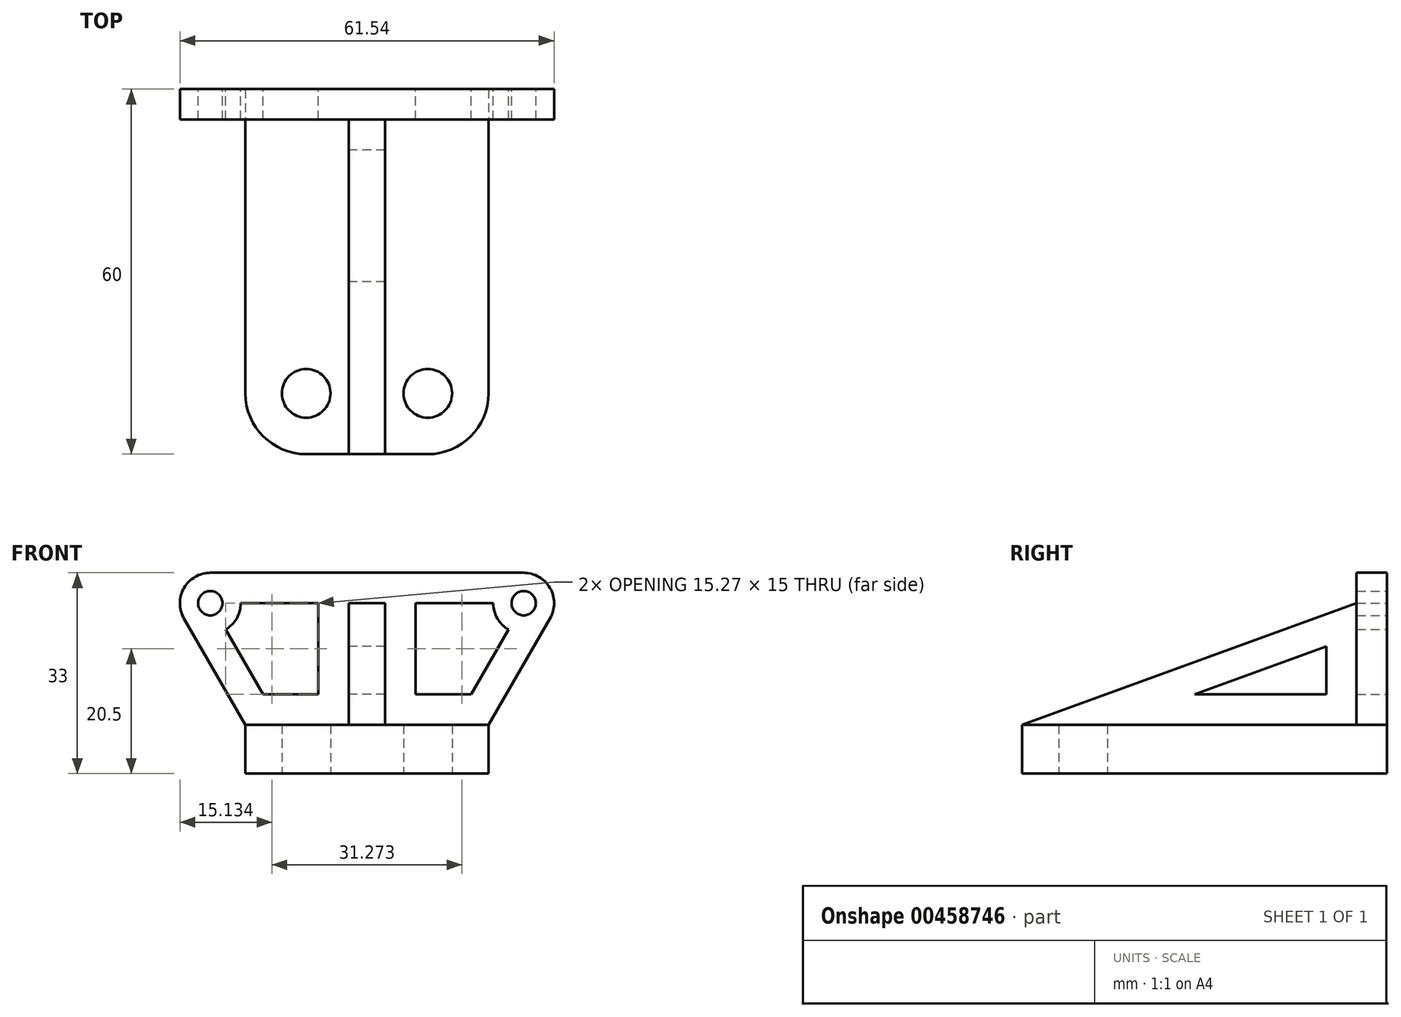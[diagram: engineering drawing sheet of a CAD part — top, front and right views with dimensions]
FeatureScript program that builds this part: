
annotation { "Feature Type Name" : "Feature", "Feature Type Description" : "" }
export const myFeature = defineFeature(function(context is Context, id is Id, definition is map)
    precondition{}
    {
        {
            var Q0;
            Q0=qCreatedBy(makeId("Top.planeOp"),FACE);
            var sketch = newSketch(context, id + "F0", { "sketchPlane" : qUnion([Q0])});
            skLineSegment(sketch, "E0.bottom", {"start": v(0, 0) * mm, "end": v(20, 0) * mm});
            skLineSegment(sketch, "E0.top", {"start": v(0, -60) * mm, "end": v(10, -60) * mm});
            skLineSegment(sketch, "E0.left", {"start": v(0, 0) * mm, "end": v(0, -60) * mm});
            skLineSegment(sketch, "E0.right", {"start": v(20, 0) * mm, "end": v(20, -50) * mm});
            skPoint(sketch, "E1.visualSharp", {"position": v(20, -60) * mm});
            skArc(sketch, "E1.filletArc", {"start": v(10, -60) * mm, "mid": v(17.07, -57.07) * mm, "end": v(20, -50) * mm});
            skCircle(sketch, "E2", {"center": v(10, -50) * mm, "radius": 4 * mm});
            skLineSegment(sketch, "E3.MirrorCS", {"start": v(0, 0) * mm, "end": v(-20, 0) * mm});
            skLineSegment(sketch, "E4.MirrorCS", {"start": v(-20, 0) * mm, "end": v(-20, -50) * mm});
            skCircle(sketch, "E5.MirrorC", {"center": v(-10, -50) * mm, "radius": 4 * mm});
            skLineSegment(sketch, "E6.MirrorCS", {"start": v(0, -60) * mm, "end": v(-10, -60) * mm});
            skArc(sketch, "E7.MirrorCS", {"start": v(-10, -60) * mm, "mid": v(-17.07, -57.07) * mm, "end": v(-20, -50) * mm});
            skSolve(sketch);
        }
        {
            var Q0;
            Q0 = qSketchRegion(id + "F0", true);
            extrude(context, id + "F1", {"entities" : qUnion([Q0]), "depth" : 8 * mm});
        }
        {
            var Q0;
            Q0=qCreatedBy(makeId("Front.planeOp"),FACE);
            var sketch = newSketch(context, id + "F2", { "sketchPlane" : qUnion([Q0])});
            skLineSegment(sketch, "E8.0", {"start": v(20, 8) * mm, "end": v(20, 0) * mm});
            skLineSegment(sketch, "E9.0", {"start": v(-20, 8) * mm, "end": v(20, 8) * mm});
            skLineSegment(sketch, "E10.0", {"start": v(-20, 0) * mm, "end": v(20, 0) * mm});
            skLineSegment(sketch, "E11.0", {"start": v(-20, 8) * mm, "end": v(-20, 0) * mm});
            skLineSegment(sketch, "E12", {"start": v(20, 8) * mm, "end": v(30.1, 25.5) * mm});
            skLineSegment(sketch, "E13", {"start": v(25.77, 33) * mm, "end": v(0, 33) * mm});
            skLineSegment(sketch, "E14", {"start": v(25.77, 28) * mm, "end": v(23.77, 28) * mm, "construction": true});
            skLineSegment(sketch, "E15", {"start": v(8, 28) * mm, "end": v(8, 13) * mm});
            skLineSegment(sketch, "E16", {"start": v(8, 13) * mm, "end": v(17.11, 13) * mm});
            skLineSegment(sketch, "E17", {"start": v(17.11, 13) * mm, "end": v(23.27, 23.67) * mm});
            skLineSegment(sketch, "E18", {"start": v(3, 28) * mm, "end": v(3, 8) * mm});
            skLineSegment(sketch, "E19", {"start": v(3, 28) * mm, "end": v(0, 28) * mm});
            skCircle(sketch, "E20", {"center": v(25.77, 28) * mm, "radius": 2 * mm});
            skPoint(sketch, "E21.visualSharp", {"position": v(34.43, 33) * mm});
            skArc(sketch, "E21.filletArc", {"start": v(30.1, 25.5) * mm, "mid": v(30.1, 30.5) * mm, "end": v(25.77, 33) * mm});
            skArc(sketch, "E22.0", {"start": v(20.77, 28) * mm, "mid": v(21.44, 25.5) * mm, "end": v(23.27, 23.67) * mm});
            skLineSegment(sketch, "E23.trimOffspring", {"start": v(20.77, 28) * mm, "end": v(8, 28) * mm});
            skLineSegment(sketch, "E24.MirrorCS", {"start": v(-25.77, 33) * mm, "end": v(0, 33) * mm});
            skLineSegment(sketch, "E25.MirrorCS", {"start": v(-3, 28) * mm, "end": v(0, 28) * mm});
            skLineSegment(sketch, "E26.MirrorCS", {"start": v(-3, 28) * mm, "end": v(-3, 8) * mm});
            skLineSegment(sketch, "E27.MirrorCS", {"start": v(-8, 28) * mm, "end": v(-8, 13) * mm});
            skLineSegment(sketch, "E28.MirrorCS", {"start": v(-20.77, 28) * mm, "end": v(-8, 28) * mm});
            skArc(sketch, "E29.MirrorCS", {"start": v(-20.77, 28) * mm, "mid": v(-21.44, 25.5) * mm, "end": v(-23.27, 23.67) * mm});
            skCircle(sketch, "E30.MirrorC", {"center": v(-25.77, 28) * mm, "radius": 2 * mm});
            skArc(sketch, "E31.MirrorCS", {"start": v(-30.1, 25.5) * mm, "mid": v(-30.1, 30.5) * mm, "end": v(-25.77, 33) * mm});
            skLineSegment(sketch, "E32.MirrorCS", {"start": v(-20, 8) * mm, "end": v(-30.1, 25.5) * mm});
            skLineSegment(sketch, "E33.MirrorCS", {"start": v(-17.11, 13) * mm, "end": v(-23.27, 23.67) * mm});
            skLineSegment(sketch, "E34.MirrorCS", {"start": v(-8, 13) * mm, "end": v(-17.11, 13) * mm});
            skSolve(sketch);
        }
        {
            var Q0;
            {var subQ0=sQuery(id+"F2.wireOp",EDGE,"E18");Q0=makeQuery(id+"F2.imprint","IMPRINT",FACE,{"disambiguationData":[TD([[makeQuery(id+"F2.imprint","IMPRINT",EDGE,{"derivedFrom":subQ0}),-1.0]])]});}
            var Q1;
            {var subQ2=sQuery(id+"F2.wireOp",EDGE,"E12");Q1=makeQuery(id+"F2.imprint","IMPRINT",FACE,{"disambiguationData":[TD([[makeQuery(id+"F2.imprint","IMPRINT",EDGE,{"derivedFrom":subQ2}),1.0]])]});}
            extrude(context, id + "F3", {"entities" : qUnion([Q0, Q1]), "operationType" : NewBodyOperationType.ADD, "depth" : 5 * mm});
        }
        {
            var Q0;
            Q0=qCreatedBy(makeId("Right.planeOp"),FACE);
            var sketch = newSketch(context, id + "F4", { "sketchPlane" : qUnion([Q0])});
            skLineSegment(sketch, "E35.0.1", {"start": v(-5, 8) * mm, "end": v(-50, 8) * mm});
            skLineSegment(sketch, "E35.0.2", {"start": v(-50, 8) * mm, "end": v(-60, 8) * mm});
            skLineSegment(sketch, "E35.0.4", {"start": v(-60, 8) * mm, "end": v(-50, 8) * mm});
            skLineSegment(sketch, "E35.0.5", {"start": v(-50, 8) * mm, "end": v(-5, 8) * mm});
            skLineSegment(sketch, "E36.0.0", {"start": v(-5, 25.5) * mm, "end": v(-5, 8) * mm});
            skLineSegment(sketch, "E36.0.2", {"start": v(-5, 8) * mm, "end": v(-5, 25.5) * mm});
            skLineSegment(sketch, "E36.0.3", {"start": v(-5, 25.5) * mm, "end": v(-5, 33) * mm});
            skLineSegment(sketch, "E36.0.5", {"start": v(-5, 33) * mm, "end": v(-5, 25.5) * mm});
            skLineSegment(sketch, "E37", {"start": v(-5, 28.02) * mm, "end": v(-60, 8) * mm});
            skLineSegment(sketch, "E38.0", {"start": v(-10, 20.88) * mm, "end": v(-31.64, 13) * mm});
            skLineSegment(sketch, "E38.1", {"start": v(-10, 13) * mm, "end": v(-10, 20.88) * mm});
            skLineSegment(sketch, "E38.2", {"start": v(-31.64, 13) * mm, "end": v(-10, 13) * mm});
            skSolve(sketch);
        }
        {
            var Q0;
            Q0 = qSketchRegion(id + "F4", true);
            extrude(context, id + "F5", {"entities" : qUnion([Q0]), "operationType" : NewBodyOperationType.ADD, "depth" : 6 * mm, "symmetric" : true});
        }
    });
